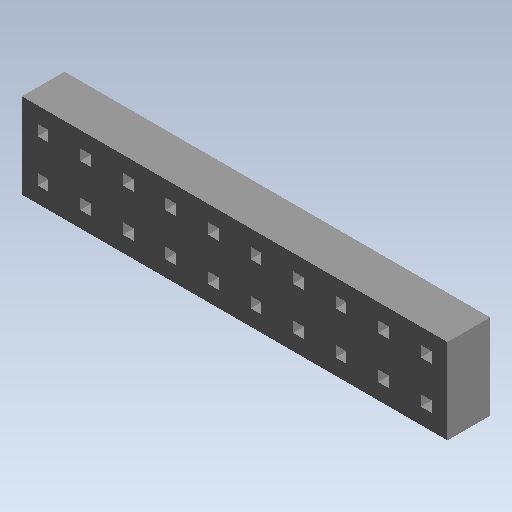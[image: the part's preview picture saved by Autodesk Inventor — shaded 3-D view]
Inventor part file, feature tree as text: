
AUTODESK INVENTOR PART (.ipt)
format: ipt  version: 2021 (Build 250183000, 183)  size: 186,880 bytes
history: native  units: mm (DEFAULTED — no unit token found)
features: other x7, extrude x1
ambient origin geometry x8: Origin, YZ Plane, XZ Plane, XY Plane, X Axis, Y Axis, Z Axis, Center Point
bodies: Solid1 (feature_tree)
feature tree (8):
  extrude  "Extrusion1"  Depth=2.0066mm TaperAngle=0.0deg
  other  "0_XY"
  other  "0_YZ"
  other  "0_ZX"
  other  "0_X"
  other  "0_Y"
  other  "0_Z"
  other  "0_Center"
